# Revit family: Bolzenanker BZ-IG, vz
name_source: partatom
category: HLS-Bauteile
revit_build: Autodesk Revit 2017 (Build: 20190507_1515(x64)
units: mm (PartAtom-declared; Revit-internal decimal feet)

## family parameters
Basisbauteil = Fläche
Beim Laden mit Abzugskörper schneiden = Nein
Bemaßung runder Anschluss = Durchmesser verwenden
Gemeinsam genutzt = Ja
Raumberechnungspunkt = Nein
Teiletyp = Normal

## types (3) — shared parameters
Fabrikat = MKT
Firma = MEFA Befestigungs- und Montagesysteme GmbH
Kurztext1 = Bolzenanker BZ IG
Material = Stahl
Mengeneinheit = St
Vorgabe-Ansicht = 1219 mm

## per-type parameters (varying)
| type | Artikelnummer | Bohrlochtiefe | D | EAN | Gewicht | Gewicht pro Bauteil | Gewinde | Kurztext2 | Länge | Länge Dübel | Länge Gewinde | T | Verankerungstiefe | d1 | vpe |
| Bolzenanker BZ-IG M 8-0, gvz | 2218036101 | 75 mm | 3 mm  [stored 0.00984252 ft] | 4043315079947 | 0.03 kg | 0.03 kg | M8 | M8 | 22 mm  [stored 0.0721785 ft] | 62 mm  [stored 0.203412 ft] | 22 mm  [stored 0.0721785 ft] | 62 mm  [stored 0.203412 ft] | 58 mm | 5 mm  [stored 0.0164042 ft] | 50 St |
| Bolzenanker BZ-IG M10-0, gvz | 2218036201 | 90 mm | 4 mm  [stored 0.0131234 ft] | 4043315079954 | 0.04 kg | 0.04 kg | M10 | M10 | 23 mm  [stored 0.0754593 ft] | 70 mm  [stored 0.229659 ft] | 23 mm  [stored 0.0754593 ft] | 70 mm  [stored 0.229659 ft] | 65 mm | 6 mm  [stored 0.019685 ft] | 25 St |
| Bolzenanker BZ-IG M12-0, gvz | 2218036301 | 105 mm | 5 mm  [stored 0.0164042 ft] | 4043315079961 | 0.10 kg | 0.10 kg | M12 | M12 | 27 mm  [stored 0.0885827 ft] | 86 mm  [stored 0.282152 ft] | 27 mm  [stored 0.0885827 ft] | 86 mm  [stored 0.282152 ft] | 80 mm | 8 mm  [stored 0.0262467 ft] | 20 St |

note: [stored X ft] marks values corroborated as IEEE doubles in the binary element streams (Revit-internal decimal feet)
